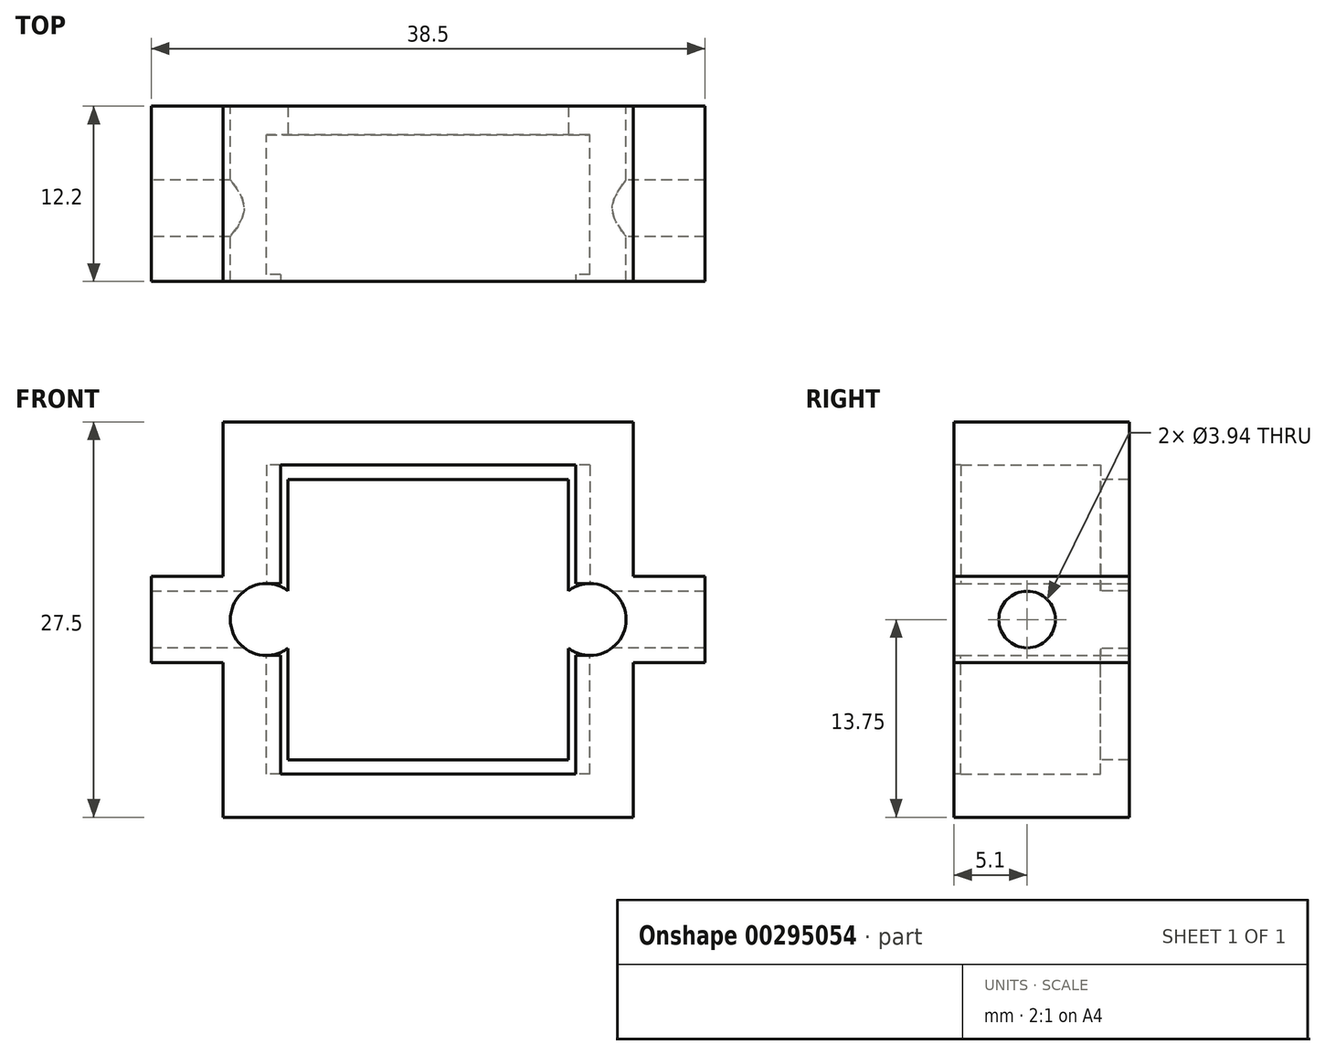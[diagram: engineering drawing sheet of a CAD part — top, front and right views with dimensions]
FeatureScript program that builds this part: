
annotation { "Feature Type Name" : "Feature", "Feature Type Description" : "" }
export const myFeature = defineFeature(function(context is Context, id is Id, definition is map)
    precondition{}
    {
        {
            var Q0;
            Q0=qCreatedBy(makeId("Front.planeOp"),FACE);
            var sketch = newSketch(context, id + "F0", { "sketchPlane" : qUnion([Q0])});
            skLineSegment(sketch, "E0", {"start": v(-19.25, 3) * mm, "end": v(-14.25, 3) * mm});
            skLineSegment(sketch, "E1", {"start": v(-14.25, 3) * mm, "end": v(-14.25, 13.75) * mm});
            skLineSegment(sketch, "E2", {"start": v(-14.25, 13.75) * mm, "end": v(0, 13.75) * mm});
            skLineSegment(sketch, "E3", {"start": v(0, 13.75) * mm, "end": v(0, 10.75) * mm});
            skLineSegment(sketch, "E4", {"start": v(0, 10.75) * mm, "end": v(-11.25, 10.75) * mm});
            skLineSegment(sketch, "E5", {"start": v(-19.25, 3) * mm, "end": v(-19.25, 0) * mm});
            skLineSegment(sketch, "E6", {"start": v(-19.25, 0) * mm, "end": v(-13.75, 0) * mm});
            skLineSegment(sketch, "E7", {"start": v(-11.25, 10.75) * mm, "end": v(-11.25, 2.5) * mm});
            skArc(sketch, "E8", {"start": v(-13.75, 0) * mm, "mid": v(-13.02, 1.77) * mm, "end": v(-11.25, 2.5) * mm});
            skLineSegment(sketch, "E9.MirrorCS", {"start": v(19.25, 3) * mm, "end": v(19.25, 0) * mm});
            skLineSegment(sketch, "E10.MirrorCS", {"start": v(19.25, 3) * mm, "end": v(14.25, 3) * mm});
            skLineSegment(sketch, "E11.MirrorCS", {"start": v(11.25, 10.75) * mm, "end": v(11.25, 2.5) * mm});
            skLineSegment(sketch, "E12.MirrorCS", {"start": v(19.25, 0) * mm, "end": v(13.75, 0) * mm});
            skArc(sketch, "E13.MirrorCS", {"start": v(13.75, 0) * mm, "mid": v(13.02, 1.77) * mm, "end": v(11.25, 2.5) * mm});
            skLineSegment(sketch, "E14.MirrorCS", {"start": v(14.25, 3) * mm, "end": v(14.25, 13.75) * mm});
            skLineSegment(sketch, "E15.MirrorCS", {"start": v(0, 10.75) * mm, "end": v(11.25, 10.75) * mm});
            skLineSegment(sketch, "E16.MirrorCS", {"start": v(14.25, 13.75) * mm, "end": v(0, 13.75) * mm});
            skLineSegment(sketch, "E17.MirrorCS", {"start": v(19.25, -3) * mm, "end": v(19.25, 0) * mm});
            skLineSegment(sketch, "E18.MirrorCS", {"start": v(0, -13.75) * mm, "end": v(0, -10.75) * mm});
            skArc(sketch, "E19.MirrorCS", {"start": v(13.75, 0) * mm, "mid": v(13.02, -1.77) * mm, "end": v(11.25, -2.5) * mm});
            skArc(sketch, "E20.MirrorCS", {"start": v(-13.75, 0) * mm, "mid": v(-13.02, -1.77) * mm, "end": v(-11.25, -2.5) * mm});
            skLineSegment(sketch, "E21.MirrorCS", {"start": v(-19.25, -3) * mm, "end": v(-19.25, 0) * mm});
            skLineSegment(sketch, "E22.MirrorCS", {"start": v(14.25, -13.75) * mm, "end": v(0, -13.75) * mm});
            skLineSegment(sketch, "E23.MirrorCS", {"start": v(11.25, -10.75) * mm, "end": v(11.25, -2.5) * mm});
            skLineSegment(sketch, "E24.MirrorCS", {"start": v(-11.25, -10.75) * mm, "end": v(-11.25, -2.5) * mm});
            skLineSegment(sketch, "E25.MirrorCS", {"start": v(-14.25, -13.75) * mm, "end": v(0, -13.75) * mm});
            skLineSegment(sketch, "E26.MirrorCS", {"start": v(-14.25, -3) * mm, "end": v(-14.25, -13.75) * mm});
            skLineSegment(sketch, "E27.MirrorCS", {"start": v(-19.25, -3) * mm, "end": v(-14.25, -3) * mm});
            skLineSegment(sketch, "E28.MirrorCS", {"start": v(14.25, -3) * mm, "end": v(14.25, -13.75) * mm});
            skLineSegment(sketch, "E29.MirrorCS", {"start": v(0, -10.75) * mm, "end": v(11.25, -10.75) * mm});
            skLineSegment(sketch, "E30.MirrorCS", {"start": v(19.25, -3) * mm, "end": v(14.25, -3) * mm});
            skLineSegment(sketch, "E31.MirrorCS", {"start": v(0, -10.75) * mm, "end": v(-11.25, -10.75) * mm});
            skSolve(sketch);
        }
        {
            var Q0;
            Q0=qSketchRegion(id+"F0",true);
            extrude(context, id + "F1", {"entities" : qUnion([Q0]), "depth" : 10.2 * mm});
        }
        {
            var Q0;
            Q0=makeQuery(id+"F1.opExtrude","CAP_FACE",FACE,{"disambiguationData":[OSD([sQuery(id+"F0.wireOp",EDGE,"E0"),sQuery(id+"F0.wireOp",EDGE,"E1"),sQuery(id+"F0.wireOp",EDGE,"E2"),sQuery(id+"F0.wireOp",EDGE,"E4"),sQuery(id+"F0.wireOp",EDGE,"E5"),sQuery(id+"F0.wireOp",EDGE,"E7"),sQuery(id+"F0.wireOp",EDGE,"E8"),sQuery(id+"F0.wireOp",EDGE,"E9.MirrorCS"),sQuery(id+"F0.wireOp",EDGE,"E10.MirrorCS"),sQuery(id+"F0.wireOp",EDGE,"E11.MirrorCS"),sQuery(id+"F0.wireOp",EDGE,"E13.MirrorCS"),sQuery(id+"F0.wireOp",EDGE,"E14.MirrorCS"),sQuery(id+"F0.wireOp",EDGE,"E15.MirrorCS"),sQuery(id+"F0.wireOp",EDGE,"E16.MirrorCS"),sQuery(id+"F0.wireOp",EDGE,"E17.MirrorCS"),sQuery(id+"F0.wireOp",EDGE,"E19.MirrorCS"),sQuery(id+"F0.wireOp",EDGE,"E20.MirrorCS"),sQuery(id+"F0.wireOp",EDGE,"E21.MirrorCS"),sQuery(id+"F0.wireOp",EDGE,"E22.MirrorCS"),sQuery(id+"F0.wireOp",EDGE,"E23.MirrorCS"),sQuery(id+"F0.wireOp",EDGE,"E24.MirrorCS"),sQuery(id+"F0.wireOp",EDGE,"E25.MirrorCS"),sQuery(id+"F0.wireOp",EDGE,"E26.MirrorCS"),sQuery(id+"F0.wireOp",EDGE,"E27.MirrorCS"),sQuery(id+"F0.wireOp",EDGE,"E28.MirrorCS"),sQuery(id+"F0.wireOp",EDGE,"E29.MirrorCS"),sQuery(id+"F0.wireOp",EDGE,"E30.MirrorCS"),sQuery(id+"F0.wireOp",EDGE,"E31.MirrorCS")])],"isStart":true});
            var sketch = newSketch(context, id + "F2", { "sketchPlane" : qUnion([Q0])});
            skLineSegment(sketch, "E32.bottom", {"start": v(14.25, -13.75) * mm, "end": v(-14.25, -13.75) * mm});
            skLineSegment(sketch, "E32.top", {"start": v(14.25, 13.75) * mm, "end": v(-14.25, 13.75) * mm});
            skLineSegment(sketch, "E32.left", {"start": v(14.25, -13.75) * mm, "end": v(14.25, 13.75) * mm});
            skLineSegment(sketch, "E32.right", {"start": v(-14.25, -13.75) * mm, "end": v(-14.25, 13.75) * mm});
            skPoint(sketch, "E32.middle", {"position": v(0, 0) * mm});
            skLineSegment(sketch, "E33.bottom", {"start": v(9.75, -9.75) * mm, "end": v(-9.75, -9.75) * mm});
            skLineSegment(sketch, "E33.top", {"start": v(9.75, 9.75) * mm, "end": v(-9.75, 9.75) * mm});
            skLineSegment(sketch, "E33.left", {"start": v(9.75, -9.75) * mm, "end": v(9.75, 9.75) * mm});
            skLineSegment(sketch, "E33.right", {"start": v(-9.75, -9.75) * mm, "end": v(-9.75, 9.75) * mm});
            skSolve(sketch);
        }
        {
            var Q0;
            Q0=qSketchRegion(id+"F2",true);
            extrude(context, id + "F3", {"entities" : qUnion([Q0]), "operationType" : NewBodyOperationType.ADD, "depth" : 2 * mm});
        }
        {
            var Q0;
            Q0=makeQuery(id+"F1.opExtrude","SWEPT_FACE",FACE,{"disambiguationData":[OSD([sQuery(id+"F0.wireOp",EDGE,"E5"),sQuery(id+"F0.wireOp",EDGE,"E21.MirrorCS")])]});
            var sketch = newSketch(context, id + "F4", { "sketchPlane" : qUnion([Q0])});
            skCircle(sketch, "E34", {"center": v(5.1, 0) * mm, "radius": 1.97 * mm});
            skLineSegment(sketch, "E35", {"start": v(0, 0) * mm, "end": v(5.1, 0) * mm, "construction": true});
            skLineSegment(sketch, "E36", {"start": v(5.1, 0) * mm, "end": v(10.2, 0) * mm, "construction": true});
            skSolve(sketch);
        }
        {
            var Q0;
            Q0=qSketchRegion(id+"F4",true);
            var Q1;
            Q1=makeQuery(id+"F1.opExtrude","SWEPT_FACE",FACE,{"disambiguationData":[OSD([sQuery(id+"F0.wireOp",EDGE,"E9.MirrorCS"),sQuery(id+"F0.wireOp",EDGE,"E17.MirrorCS")])]});
            extrude(context, id + "F5", {"entities" : qUnion([Q0]), "operationType" : NewBodyOperationType.REMOVE, "endBound" : BoundingType.UP_TO_SURFACE, "oppositeDirection" : true, "endBoundEntityFace" : qUnion([Q1]), "depth" : 25.4 * mm});
        }
        {
            var Q0;
            {var subQ0=sQuery(id+"F0.wireOp",EDGE,"E14.MirrorCS");var subQ1=sQuery(id+"F0.wireOp",EDGE,"E10.MirrorCS");var subQ2=sQuery(id+"F0.wireOp",EDGE,"E30.MirrorCS");var subQ3=sQuery(id+"F0.wireOp",EDGE,"E28.MirrorCS");var subQ4=sQuery(id+"F0.wireOp",EDGE,"E17.MirrorCS");var subQ5=sQuery(id+"F0.wireOp",EDGE,"E9.MirrorCS");Q0=makeQuery(id+"F3.boolean.opBoolean","SPLIT",FACE,{"disambiguationData":[TD([makeQuery(id+"F1.opExtrude","SWEPT_FACE",FACE,{"disambiguationData":[OSD([subQ1])]})])],"derivedFrom":makeQuery(id+"F1.opExtrude","CAP_FACE",FACE,{"disambiguationData":[OSD([sQuery(id+"F0.wireOp",EDGE,"E0"),sQuery(id+"F0.wireOp",EDGE,"E1"),sQuery(id+"F0.wireOp",EDGE,"E2"),sQuery(id+"F0.wireOp",EDGE,"E4"),sQuery(id+"F0.wireOp",EDGE,"E5"),sQuery(id+"F0.wireOp",EDGE,"E7"),sQuery(id+"F0.wireOp",EDGE,"E8"),subQ5,subQ1,sQuery(id+"F0.wireOp",EDGE,"E11.MirrorCS"),sQuery(id+"F0.wireOp",EDGE,"E13.MirrorCS"),subQ0,sQuery(id+"F0.wireOp",EDGE,"E15.MirrorCS"),sQuery(id+"F0.wireOp",EDGE,"E16.MirrorCS"),subQ4,sQuery(id+"F0.wireOp",EDGE,"E19.MirrorCS"),sQuery(id+"F0.wireOp",EDGE,"E20.MirrorCS"),sQuery(id+"F0.wireOp",EDGE,"E21.MirrorCS"),sQuery(id+"F0.wireOp",EDGE,"E22.MirrorCS"),sQuery(id+"F0.wireOp",EDGE,"E23.MirrorCS"),sQuery(id+"F0.wireOp",EDGE,"E24.MirrorCS"),sQuery(id+"F0.wireOp",EDGE,"E25.MirrorCS"),sQuery(id+"F0.wireOp",EDGE,"E26.MirrorCS"),sQuery(id+"F0.wireOp",EDGE,"E27.MirrorCS"),subQ3,sQuery(id+"F0.wireOp",EDGE,"E29.MirrorCS"),subQ2,sQuery(id+"F0.wireOp",EDGE,"E31.MirrorCS")])],"isStart":true})});}
            var sketch = newSketch(context, id + "F6", { "sketchPlane" : qUnion([Q0])});
            skLineSegment(sketch, "E37.bottom", {"start": v(-19.25, -3) * mm, "end": v(-14.25, -3) * mm});
            skLineSegment(sketch, "E37.top", {"start": v(-19.25, 3) * mm, "end": v(-14.25, 3) * mm});
            skLineSegment(sketch, "E37.left", {"start": v(-19.25, -3) * mm, "end": v(-19.25, 3) * mm});
            skLineSegment(sketch, "E37.right", {"start": v(-14.25, -3) * mm, "end": v(-14.25, 3) * mm});
            skSolve(sketch);
        }
        {
            var Q0;
            Q0=qSketchRegion(id+"F6",true);
            var Q1;
            Q1=makeQuery(id+"F3.opExtrude","CAP_FACE",FACE,{"disambiguationData":[OSD([sQuery(id+"F2.wireOp",EDGE,"E32.bottom"),sQuery(id+"F2.wireOp",EDGE,"E32.top"),sQuery(id+"F2.wireOp",EDGE,"E32.left"),sQuery(id+"F2.wireOp",EDGE,"E32.right"),sQuery(id+"F2.wireOp",EDGE,"E33.bottom"),sQuery(id+"F2.wireOp",EDGE,"E33.top"),sQuery(id+"F2.wireOp",EDGE,"E33.left"),sQuery(id+"F2.wireOp",EDGE,"E33.right")])],"isStart":false});
            extrude(context, id + "F7", {"entities" : qUnion([Q0]), "operationType" : NewBodyOperationType.ADD, "endBound" : BoundingType.UP_TO_SURFACE, "endBoundEntityFace" : qUnion([Q1]), "depth" : 25.4 * mm});
        }
        {
            var Q0;
            {var subQ0=sQuery(id+"F0.wireOp",EDGE,"E26.MirrorCS");var subQ1=sQuery(id+"F0.wireOp",EDGE,"E21.MirrorCS");var subQ2=sQuery(id+"F0.wireOp",EDGE,"E5");var subQ3=sQuery(id+"F0.wireOp",EDGE,"E1");var subQ4=sQuery(id+"F0.wireOp",EDGE,"E0");var subQ5=sQuery(id+"F0.wireOp",EDGE,"E27.MirrorCS");Q0=makeQuery(id+"F3.boolean.opBoolean","SPLIT",FACE,{"disambiguationData":[TD([makeQuery(id+"F1.opExtrude","SWEPT_FACE",FACE,{"disambiguationData":[OSD([subQ4])]})])],"derivedFrom":makeQuery(id+"F1.opExtrude","CAP_FACE",FACE,{"disambiguationData":[OSD([subQ4,subQ3,sQuery(id+"F0.wireOp",EDGE,"E2"),sQuery(id+"F0.wireOp",EDGE,"E4"),subQ2,sQuery(id+"F0.wireOp",EDGE,"E7"),sQuery(id+"F0.wireOp",EDGE,"E8"),sQuery(id+"F0.wireOp",EDGE,"E9.MirrorCS"),sQuery(id+"F0.wireOp",EDGE,"E10.MirrorCS"),sQuery(id+"F0.wireOp",EDGE,"E11.MirrorCS"),sQuery(id+"F0.wireOp",EDGE,"E13.MirrorCS"),sQuery(id+"F0.wireOp",EDGE,"E14.MirrorCS"),sQuery(id+"F0.wireOp",EDGE,"E15.MirrorCS"),sQuery(id+"F0.wireOp",EDGE,"E16.MirrorCS"),sQuery(id+"F0.wireOp",EDGE,"E17.MirrorCS"),sQuery(id+"F0.wireOp",EDGE,"E19.MirrorCS"),sQuery(id+"F0.wireOp",EDGE,"E20.MirrorCS"),subQ1,sQuery(id+"F0.wireOp",EDGE,"E22.MirrorCS"),sQuery(id+"F0.wireOp",EDGE,"E23.MirrorCS"),sQuery(id+"F0.wireOp",EDGE,"E24.MirrorCS"),sQuery(id+"F0.wireOp",EDGE,"E25.MirrorCS"),subQ0,subQ5,sQuery(id+"F0.wireOp",EDGE,"E28.MirrorCS"),sQuery(id+"F0.wireOp",EDGE,"E29.MirrorCS"),sQuery(id+"F0.wireOp",EDGE,"E30.MirrorCS"),sQuery(id+"F0.wireOp",EDGE,"E31.MirrorCS")])],"isStart":true})});}
            var sketch = newSketch(context, id + "F8", { "sketchPlane" : qUnion([Q0])});
            skLineSegment(sketch, "E38.bottom", {"start": v(19.25, -3) * mm, "end": v(14.25, -3) * mm});
            skLineSegment(sketch, "E38.top", {"start": v(19.25, 3) * mm, "end": v(14.25, 3) * mm});
            skLineSegment(sketch, "E38.left", {"start": v(19.25, -3) * mm, "end": v(19.25, 3) * mm});
            skLineSegment(sketch, "E38.right", {"start": v(14.25, -3) * mm, "end": v(14.25, 3) * mm});
            skSolve(sketch);
        }
        {
            var Q0;
            Q0=qSketchRegion(id+"F8",true);
            var Q1;
            {var subQ0=sQuery(id+"F2.wireOp",EDGE,"E33.right");var subQ1=sQuery(id+"F2.wireOp",EDGE,"E33.left");var subQ2=sQuery(id+"F2.wireOp",EDGE,"E33.top");var subQ3=sQuery(id+"F2.wireOp",EDGE,"E33.bottom");var subQ4=sQuery(id+"F2.wireOp",EDGE,"E32.right");var subQ5=sQuery(id+"F2.wireOp",EDGE,"E32.left");var subQ6=sQuery(id+"F2.wireOp",EDGE,"E32.top");var subQ7=sQuery(id+"F2.wireOp",EDGE,"E32.bottom");Q1=makeQuery(id+"F7.boolean.opBoolean","MERGE",FACE,{"derivedFrom":[makeQuery(id+"F3.opExtrude","CAP_FACE",FACE,{"disambiguationData":[OSD([subQ7,subQ6,subQ5,subQ4,subQ3,subQ2,subQ1,subQ0])],"isStart":false}),makeQuery(id+"F7.opExtrude","CAP_FACE",FACE,{"disambiguationData":[OSD([subQ7,subQ6,subQ5,subQ4,subQ3,subQ2,subQ1,subQ0])],"isStart":false})]});}
            extrude(context, id + "F9", {"entities" : qUnion([Q0]), "operationType" : NewBodyOperationType.ADD, "endBound" : BoundingType.UP_TO_SURFACE, "endBoundEntityFace" : qUnion([Q1]), "depth" : 25.4 * mm});
        }
        {
            var Q0;
            Q0=makeQuery(id+"F1.opExtrude","CAP_FACE",FACE,{"disambiguationData":[OSD([sQuery(id+"F0.wireOp",EDGE,"E0"),sQuery(id+"F0.wireOp",EDGE,"E1"),sQuery(id+"F0.wireOp",EDGE,"E2"),sQuery(id+"F0.wireOp",EDGE,"E4"),sQuery(id+"F0.wireOp",EDGE,"E5"),sQuery(id+"F0.wireOp",EDGE,"E7"),sQuery(id+"F0.wireOp",EDGE,"E8"),sQuery(id+"F0.wireOp",EDGE,"E9.MirrorCS"),sQuery(id+"F0.wireOp",EDGE,"E10.MirrorCS"),sQuery(id+"F0.wireOp",EDGE,"E11.MirrorCS"),sQuery(id+"F0.wireOp",EDGE,"E13.MirrorCS"),sQuery(id+"F0.wireOp",EDGE,"E14.MirrorCS"),sQuery(id+"F0.wireOp",EDGE,"E15.MirrorCS"),sQuery(id+"F0.wireOp",EDGE,"E16.MirrorCS"),sQuery(id+"F0.wireOp",EDGE,"E17.MirrorCS"),sQuery(id+"F0.wireOp",EDGE,"E19.MirrorCS"),sQuery(id+"F0.wireOp",EDGE,"E20.MirrorCS"),sQuery(id+"F0.wireOp",EDGE,"E21.MirrorCS"),sQuery(id+"F0.wireOp",EDGE,"E22.MirrorCS"),sQuery(id+"F0.wireOp",EDGE,"E23.MirrorCS"),sQuery(id+"F0.wireOp",EDGE,"E24.MirrorCS"),sQuery(id+"F0.wireOp",EDGE,"E25.MirrorCS"),sQuery(id+"F0.wireOp",EDGE,"E26.MirrorCS"),sQuery(id+"F0.wireOp",EDGE,"E27.MirrorCS"),sQuery(id+"F0.wireOp",EDGE,"E28.MirrorCS"),sQuery(id+"F0.wireOp",EDGE,"E29.MirrorCS"),sQuery(id+"F0.wireOp",EDGE,"E30.MirrorCS"),sQuery(id+"F0.wireOp",EDGE,"E31.MirrorCS")])],"isStart":false});
            var sketch = newSketch(context, id + "F10", { "sketchPlane" : qUnion([Q0])});
            skLineSegment(sketch, "E39.bottom", {"start": v(-11.25, 2.5) * mm, "end": v(-10.25, 2.5) * mm});
            skLineSegment(sketch, "E39.top", {"start": v(-11.25, 10.75) * mm, "end": v(-10.25, 10.75) * mm});
            skLineSegment(sketch, "E39.left", {"start": v(-11.25, 2.5) * mm, "end": v(-11.25, 10.75) * mm});
            skLineSegment(sketch, "E39.right", {"start": v(-10.25, 2.5) * mm, "end": v(-10.25, 10.75) * mm});
            skLineSegment(sketch, "E40.MirrorCS", {"start": v(11.25, 10.75) * mm, "end": v(10.25, 10.75) * mm});
            skLineSegment(sketch, "E41.MirrorCS", {"start": v(11.25, 2.5) * mm, "end": v(10.25, 2.5) * mm});
            skLineSegment(sketch, "E42.MirrorCS", {"start": v(11.25, 2.5) * mm, "end": v(11.25, 10.75) * mm});
            skLineSegment(sketch, "E43.MirrorCS", {"start": v(10.25, 2.5) * mm, "end": v(10.25, 10.75) * mm});
            skLineSegment(sketch, "E44.MirrorCS", {"start": v(-11.25, -2.5) * mm, "end": v(-10.25, -2.5) * mm});
            skLineSegment(sketch, "E45.MirrorCS", {"start": v(-11.25, -10.75) * mm, "end": v(-10.25, -10.75) * mm});
            skLineSegment(sketch, "E46.MirrorCS", {"start": v(11.25, -2.5) * mm, "end": v(10.25, -2.5) * mm});
            skLineSegment(sketch, "E47.MirrorCS", {"start": v(11.25, -10.75) * mm, "end": v(10.25, -10.75) * mm});
            skLineSegment(sketch, "E48.MirrorCS", {"start": v(-11.25, -2.5) * mm, "end": v(-11.25, -10.75) * mm});
            skLineSegment(sketch, "E49.MirrorCS", {"start": v(-10.25, -2.5) * mm, "end": v(-10.25, -10.75) * mm});
            skLineSegment(sketch, "E50.MirrorCS", {"start": v(11.25, -2.5) * mm, "end": v(11.25, -10.75) * mm});
            skLineSegment(sketch, "E51.MirrorCS", {"start": v(10.25, -2.5) * mm, "end": v(10.25, -10.75) * mm});
            skSolve(sketch);
        }
        {
            var Q0;
            Q0 = qSketchRegion(id + "F10", true);
            extrude(context, id + "F11", {"entities" : qUnion([Q0]), "operationType" : NewBodyOperationType.ADD, "oppositeDirection" : true, "depth" : 0.5 * mm});
        }
        {
            var Q0;
            Q0=makeQuery(id+"F11.boolean.opBoolean","MERGE",FACE,{"derivedFrom":[makeQuery(id+"F1.opExtrude","CAP_FACE",FACE,{"disambiguationData":[OSD([sQuery(id+"F0.wireOp",EDGE,"E0"),sQuery(id+"F0.wireOp",EDGE,"E1"),sQuery(id+"F0.wireOp",EDGE,"E2"),sQuery(id+"F0.wireOp",EDGE,"E4"),sQuery(id+"F0.wireOp",EDGE,"E5"),sQuery(id+"F0.wireOp",EDGE,"E7"),sQuery(id+"F0.wireOp",EDGE,"E8"),sQuery(id+"F0.wireOp",EDGE,"E9.MirrorCS"),sQuery(id+"F0.wireOp",EDGE,"E10.MirrorCS"),sQuery(id+"F0.wireOp",EDGE,"E11.MirrorCS"),sQuery(id+"F0.wireOp",EDGE,"E13.MirrorCS"),sQuery(id+"F0.wireOp",EDGE,"E14.MirrorCS"),sQuery(id+"F0.wireOp",EDGE,"E15.MirrorCS"),sQuery(id+"F0.wireOp",EDGE,"E16.MirrorCS"),sQuery(id+"F0.wireOp",EDGE,"E17.MirrorCS"),sQuery(id+"F0.wireOp",EDGE,"E19.MirrorCS"),sQuery(id+"F0.wireOp",EDGE,"E20.MirrorCS"),sQuery(id+"F0.wireOp",EDGE,"E21.MirrorCS"),sQuery(id+"F0.wireOp",EDGE,"E22.MirrorCS"),sQuery(id+"F0.wireOp",EDGE,"E23.MirrorCS"),sQuery(id+"F0.wireOp",EDGE,"E24.MirrorCS"),sQuery(id+"F0.wireOp",EDGE,"E25.MirrorCS"),sQuery(id+"F0.wireOp",EDGE,"E26.MirrorCS"),sQuery(id+"F0.wireOp",EDGE,"E27.MirrorCS"),sQuery(id+"F0.wireOp",EDGE,"E28.MirrorCS"),sQuery(id+"F0.wireOp",EDGE,"E29.MirrorCS"),sQuery(id+"F0.wireOp",EDGE,"E30.MirrorCS"),sQuery(id+"F0.wireOp",EDGE,"E31.MirrorCS")])],"isStart":false}),makeQuery(id+"F11.opExtrude","CAP_FACE",FACE,{"disambiguationData":[OSD([sQuery(id+"F10.wireOp",EDGE,"E39.bottom"),sQuery(id+"F10.wireOp",EDGE,"E39.top"),sQuery(id+"F10.wireOp",EDGE,"E39.left"),sQuery(id+"F10.wireOp",EDGE,"E39.right")])],"isStart":true}),makeQuery(id+"F11.opExtrude","CAP_FACE",FACE,{"disambiguationData":[OSD([sQuery(id+"F10.wireOp",EDGE,"E40.MirrorCS"),sQuery(id+"F10.wireOp",EDGE,"E41.MirrorCS"),sQuery(id+"F10.wireOp",EDGE,"E42.MirrorCS"),sQuery(id+"F10.wireOp",EDGE,"E43.MirrorCS")])],"isStart":true}),makeQuery(id+"F11.opExtrude","CAP_FACE",FACE,{"disambiguationData":[OSD([sQuery(id+"F10.wireOp",EDGE,"E44.MirrorCS"),sQuery(id+"F10.wireOp",EDGE,"E45.MirrorCS"),sQuery(id+"F10.wireOp",EDGE,"E48.MirrorCS"),sQuery(id+"F10.wireOp",EDGE,"E49.MirrorCS")])],"isStart":true}),makeQuery(id+"F11.opExtrude","CAP_FACE",FACE,{"disambiguationData":[OSD([sQuery(id+"F10.wireOp",EDGE,"E46.MirrorCS"),sQuery(id+"F10.wireOp",EDGE,"E47.MirrorCS"),sQuery(id+"F10.wireOp",EDGE,"E50.MirrorCS"),sQuery(id+"F10.wireOp",EDGE,"E51.MirrorCS")])],"isStart":true})]});
            var sketch = newSketch(context, id + "F12", { "sketchPlane" : qUnion([Q0])});
            skCircle(sketch, "E52", {"center": v(-11.25, 0) * mm, "radius": 2.5 * mm});
            skCircle(sketch, "E53.MirrorC", {"center": v(11.25, 0) * mm, "radius": 2.5 * mm});
            skSolve(sketch);
        }
        {
            var Q0;
            Q0 = qSketchRegion(id + "F12", true);
            extrude(context, id + "F13", {"entities" : qUnion([Q0]), "operationType" : NewBodyOperationType.REMOVE, "endBound" : BoundingType.THROUGH_ALL, "oppositeDirection" : true, "depth" : 25.4 * mm});
        }
    });
